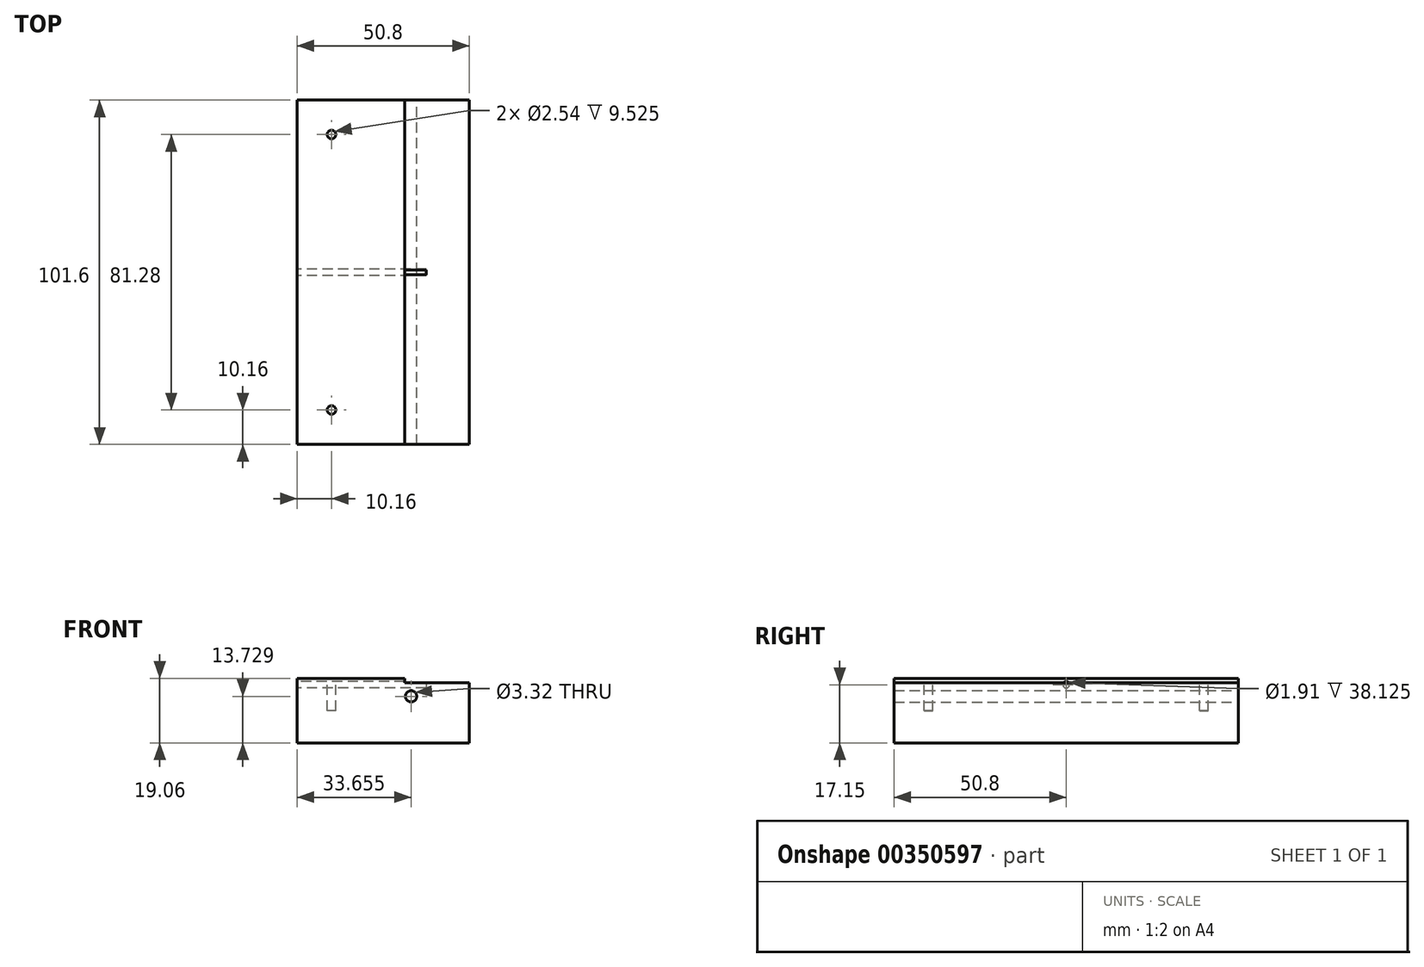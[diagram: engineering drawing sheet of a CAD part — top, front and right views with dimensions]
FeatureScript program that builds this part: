
annotation { "Feature Type Name" : "Feature", "Feature Type Description" : "" }
export const myFeature = defineFeature(function(context is Context, id is Id, definition is map)
    precondition{}
    {
        {
            var Q0;
            Q0=qCreatedBy(makeId("Front.planeOp"),FACE);
            var sketch = newSketch(context, id + "F0", { "sketchPlane" : qUnion([Q0])});
            skLineSegment(sketch, "E0.bottom", {"start": v(25.4, 9.53) * mm, "end": v(-25.4, 9.53) * mm});
            skLineSegment(sketch, "E0.top", {"start": v(25.4, -9.53) * mm, "end": v(-25.4, -9.53) * mm});
            skLineSegment(sketch, "E0.left", {"start": v(25.4, 9.53) * mm, "end": v(25.4, -9.53) * mm});
            skLineSegment(sketch, "E0.right", {"start": v(-25.4, 9.53) * mm, "end": v(-25.4, -9.53) * mm});
            skPoint(sketch, "E0.middle", {"position": v(0, 0) * mm});
            skPoint(sketch, "E1", {"position": v(6.35, 9.53) * mm});
            skLineSegment(sketch, "E2.bottom", {"start": v(6.35, 9.53) * mm, "end": v(25.4, 9.53) * mm});
            skLineSegment(sketch, "E2.top", {"start": v(6.35, 8.26) * mm, "end": v(25.4, 8.26) * mm});
            skLineSegment(sketch, "E2.left", {"start": v(6.35, 9.53) * mm, "end": v(6.35, 8.26) * mm});
            skLineSegment(sketch, "E2.right", {"start": v(25.4, 9.53) * mm, "end": v(25.4, 8.26) * mm});
            skLineSegment(sketch, "E3.bottom", {"start": v(-25.4, 6.99) * mm, "end": v(12.7, 6.99) * mm});
            skLineSegment(sketch, "E3.top", {"start": v(-25.4, 8.26) * mm, "end": v(12.7, 8.26) * mm});
            skLineSegment(sketch, "E3.left", {"start": v(-25.4, 6.99) * mm, "end": v(-25.4, 8.26) * mm});
            skLineSegment(sketch, "E3.right", {"start": v(12.7, 6.99) * mm, "end": v(12.7, 8.26) * mm});
            skCircle(sketch, "E4", {"center": v(8.25, 4.2) * mm, "radius": 1.66 * mm});
            skPoint(sketch, "E5", {"position": v(-6.35, 9.53) * mm});
            skSolve(sketch);
        }
        {
            var Q0;
            {var subQ1=sQuery(id+"F0.wireOp",EDGE,"E0.top");Q0=makeQuery(id+"F0.imprint","IMPRINT",FACE,{"disambiguationData":[TD([[makeQuery(id+"F0.imprint","IMPRINT",EDGE,{"derivedFrom":subQ1}),-1.0]])]});}
            var Q1;
            Q1=makeQuery(id+"F0.imprint","IMPRINT",FACE,{"disambiguationData":[TD([[makeQuery(id+"F0.imprint","IMPRINT",EDGE,{"derivedFrom":sQuery(id+"F0.wireOp",EDGE,"E3.bottom")}),1.0]])]});
            var Q2;
            {var subQ0=sQuery(id+"F0.wireOp",EDGE,"E0.bottom");Q2=makeQuery(id+"F0.imprint","IMPRINT",FACE,{"disambiguationData":[TD([[makeQuery(id+"F0.imprint","IMPRINT",EDGE,{"derivedFrom":subQ0}),1.0]])]});}
            extrude(context, id + "F1", {"entities" : qUnion([Q0, Q1, Q2]), "endBound" : BoundingType.SYMMETRIC, "depth" : 101.6 * mm});
        }
        {
            var Q0;
            Q0=makeQuery(id+"F1.opExtrude","SWEPT_FACE",FACE,{"disambiguationData":[OSD([sQuery(id+"F0.wireOp",EDGE,"E0.right"),sQuery(id+"F0.wireOp",EDGE,"E3.left")])]});
            var sketch = newSketch(context, id + "F2", { "sketchPlane" : qUnion([Q0])});
            skPoint(sketch, "E6", {"position": v(0, 7.62) * mm});
            skCircle(sketch, "E7", {"center": v(0, 7.62) * mm, "radius": 0.95 * mm});
            skSolve(sketch);
        }
        {
            var Q0;
            Q0=makeQuery(id+"F2.imprint","IMPRINT",FACE,{"disambiguationData":[TD([[makeQuery(id+"F2.imprint","IMPRINT",EDGE,{"derivedFrom":sQuery(id+"F2.wireOp",EDGE,"E7")}),1.0]])]});
            extrude(context, id + "F3", {"entities" : qUnion([Q0]), "operationType" : NewBodyOperationType.REMOVE, "oppositeDirection" : true, "depth" : 38.13 * mm});
        }
        {
            var Q0;
            Q0=makeQuery(id+"F1.opExtrude","SWEPT_FACE",FACE,{"disambiguationData":[OSD([sQuery(id+"F0.wireOp",EDGE,"E0.bottom")])]});
            var sketch = newSketch(context, id + "F4", { "sketchPlane" : qUnion([Q0])});
            skLineSegment(sketch, "E8", {"start": v(-15.24, 40.64) * mm, "end": v(-15.24, 0) * mm});
            skLineSegment(sketch, "E9", {"start": v(-15.24, 0) * mm, "end": v(-15.24, -40.64) * mm});
            skPoint(sketch, "E10", {"position": v(-15.24, 40.64) * mm});
            skPoint(sketch, "E11", {"position": v(-15.24, -40.64) * mm});
            skCircle(sketch, "E12", {"center": v(-15.24, -40.64) * mm, "radius": 1.27 * mm});
            skCircle(sketch, "E13", {"center": v(-15.24, 40.64) * mm, "radius": 1.27 * mm});
            skSolve(sketch);
        }
        {
            var Q0;
            Q0=makeQuery(id+"F4.imprint","IMPRINT",FACE,{"disambiguationData":[TD([[makeQuery(id+"F4.imprint","IMPRINT",EDGE,{"derivedFrom":sQuery(id+"F4.wireOp",EDGE,"E13")}),1.0]])]});
            var Q1;
            Q1=makeQuery(id+"F4.imprint","IMPRINT",FACE,{"disambiguationData":[TD([[makeQuery(id+"F4.imprint","IMPRINT",EDGE,{"derivedFrom":sQuery(id+"F4.wireOp",EDGE,"E12")}),1.0]])]});
            extrude(context, id + "F5", {"entities" : qUnion([Q0, Q1]), "operationType" : NewBodyOperationType.REMOVE, "oppositeDirection" : true, "depth" : 9.52 * mm});
        }
    });
